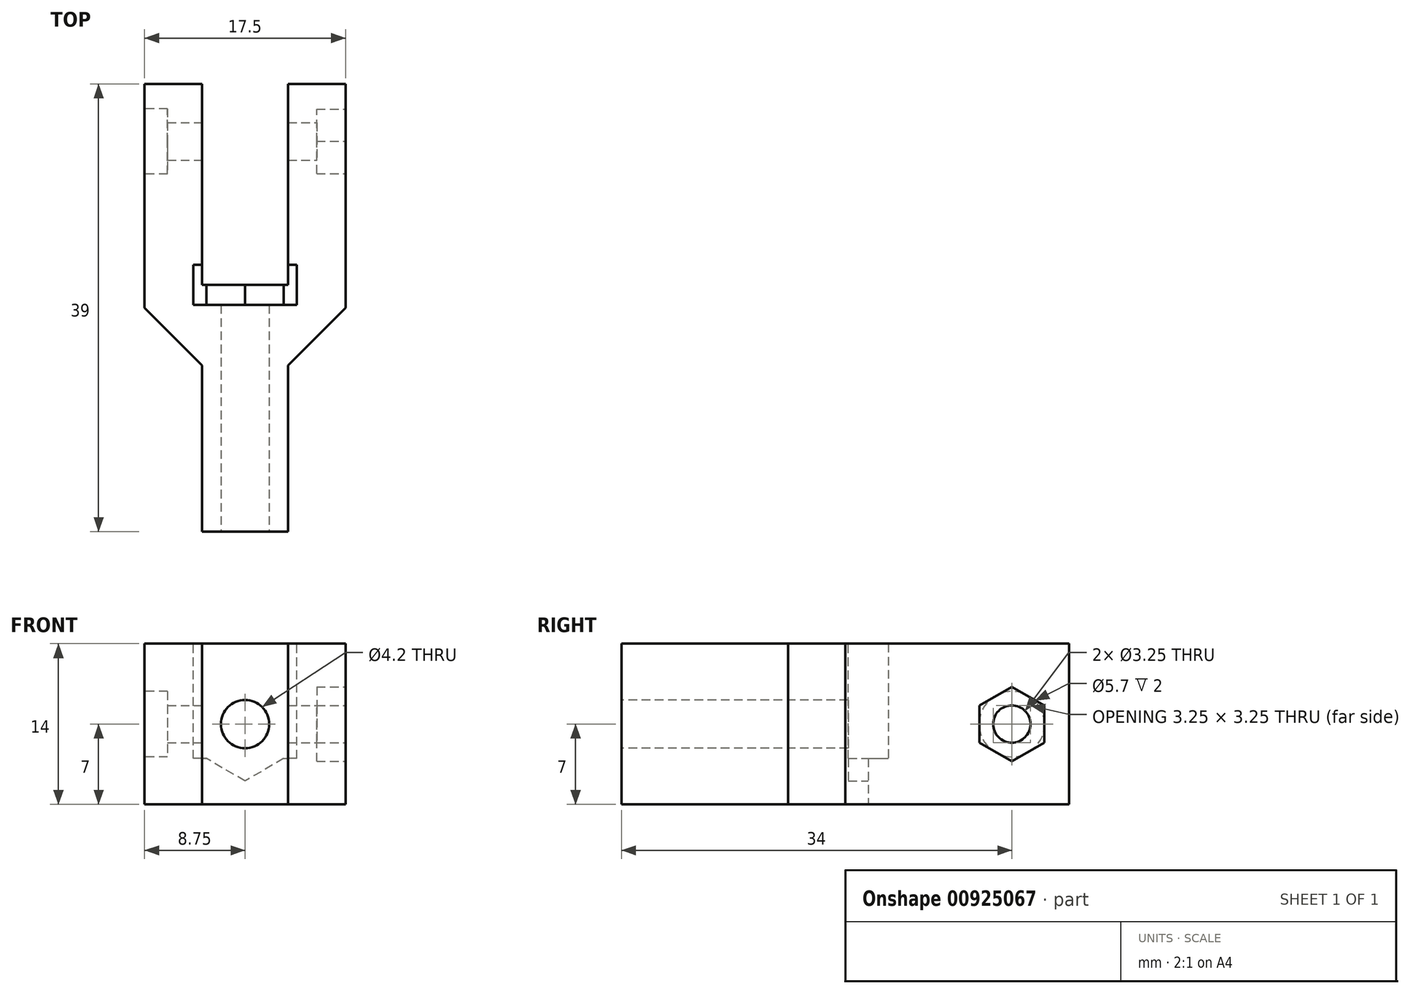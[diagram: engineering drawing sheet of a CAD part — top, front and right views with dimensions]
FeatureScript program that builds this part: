
annotation { "Feature Type Name" : "Feature", "Feature Type Description" : "" }
export const myFeature = defineFeature(function(context is Context, id is Id, definition is map)
    precondition{}
    {
        {
            var Q0;
            Q0=qCreatedBy(makeId("Top.planeOp"),FACE);
            var sketch = newSketch(context, id + "F0", { "sketchPlane" : qUnion([Q0])});
            skLineSegment(sketch, "E0.bottom", {"start": v(0, 0) * mm, "end": v(17.5, 0) * mm});
            skLineSegment(sketch, "E0.top", {"start": v(0, -39) * mm, "end": v(17.5, -39) * mm});
            skLineSegment(sketch, "E0.left", {"start": v(0, 0) * mm, "end": v(0, -39) * mm});
            skLineSegment(sketch, "E0.right", {"start": v(17.5, 0) * mm, "end": v(17.5, -39) * mm});
            skLineSegment(sketch, "E1", {"start": v(0, 0) * mm, "end": v(5, 0) * mm});
            skLineSegment(sketch, "E2", {"start": v(5, 0) * mm, "end": v(5, -17.5) * mm});
            skLineSegment(sketch, "E3", {"start": v(5, -17.5) * mm, "end": v(12.5, -17.5) * mm});
            skLineSegment(sketch, "E4", {"start": v(12.5, -17.5) * mm, "end": v(12.5, 0) * mm});
            skLineSegment(sketch, "E5", {"start": v(12.5, 0) * mm, "end": v(17.5, 0) * mm});
            skLineSegment(sketch, "E6", {"start": v(0, -19.5) * mm, "end": v(5, -24.5) * mm});
            skLineSegment(sketch, "E7", {"start": v(5, -24.5) * mm, "end": v(5, -39) * mm});
            skLineSegment(sketch, "E8", {"start": v(5, -39) * mm, "end": v(12.5, -39) * mm});
            skLineSegment(sketch, "E9", {"start": v(12.5, -39) * mm, "end": v(12.5, -24.5) * mm});
            skLineSegment(sketch, "E10", {"start": v(12.5, -24.5) * mm, "end": v(17.5, -19.5) * mm});
            skSolve(sketch);
        }
        {
            var Q0;
            {var subQ0=sQuery(id+"F0.wireOp",EDGE,"E2");Q0=makeQuery(id+"F0.imprint","IMPRINT",FACE,{"disambiguationData":[TD([[makeQuery(id+"F0.imprint","IMPRINT",EDGE,{"derivedFrom":subQ0}),-1.0]])]});}
            extrude(context, id + "F1", {"entities" : qUnion([Q0]), "depth" : 14 * mm, "offsetDistance" : 25 * mm});
        }
        {
            var Q0;
            Q0=makeQuery(id+"F1.opExtrude","SWEPT_FACE",FACE,{"disambiguationData":[OSD([sQuery(id+"F0.wireOp",EDGE,"E0.top")])]});
            var sketch = newSketch(context, id + "F2", { "sketchPlane" : qUnion([Q0])});
            skCircle(sketch, "E11", {"center": v(8.75, 7) * mm, "radius": 2.1 * mm});
            skPoint(sketch, "E11.centerSnap0", {"position": v(5, 7) * mm});
            skPoint(sketch, "E11.centerSnap1", {"position": v(8.75, 0) * mm});
            skSolve(sketch);
        }
        {
            var Q0;
            Q0 = qSketchRegion(id + "F2", true);
            extrude(context, id + "F3", {"entities" : qUnion([Q0]), "operationType" : NewBodyOperationType.REMOVE, "oppositeDirection" : true, "depth" : 25 * mm, "offsetDistance" : 25 * mm});
        }
        {
            var Q0;
            Q0=makeQuery(id+"F1.opExtrude","SWEPT_FACE",FACE,{"disambiguationData":[OSD([sQuery(id+"F0.wireOp",EDGE,"E3")])]});
            var sketch = newSketch(context, id + "F4", { "sketchPlane" : qUnion([Q0])});
            skCircle(sketch, "E12", {"center": v(-8.75, 7) * mm, "radius": 4.95 * mm});
            skLineSegment(sketch, "E13", {"start": v(-13.04, 9.48) * mm, "end": v(-13.04, 4.52) * mm});
            skLineSegment(sketch, "E14", {"start": v(-13.04, 4.52) * mm, "end": v(-8.75, 2.05) * mm});
            skLineSegment(sketch, "E15", {"start": v(-8.75, 2.05) * mm, "end": v(-4.46, 4.52) * mm});
            skLineSegment(sketch, "E16", {"start": v(-4.46, 4.52) * mm, "end": v(-4.46, 9.48) * mm});
            skLineSegment(sketch, "E17", {"start": v(-4.46, 9.48) * mm, "end": v(-8.75, 11.95) * mm});
            skLineSegment(sketch, "E18", {"start": v(-8.75, 11.95) * mm, "end": v(-13.04, 9.48) * mm});
            skSolve(sketch);
        }
        {
            var Q0;
            Q0=makeQuery(id+"F1.opExtrude","CAP_FACE",FACE,{"disambiguationData":[OSD([sQuery(id+"F0.wireOp",EDGE,"E0.bottom"),sQuery(id+"F0.wireOp",EDGE,"E0.top"),sQuery(id+"F0.wireOp",EDGE,"E0.left"),sQuery(id+"F0.wireOp",EDGE,"E0.right"),sQuery(id+"F0.wireOp",EDGE,"E2"),sQuery(id+"F0.wireOp",EDGE,"E3"),sQuery(id+"F0.wireOp",EDGE,"E4"),sQuery(id+"F0.wireOp",EDGE,"E6"),sQuery(id+"F0.wireOp",EDGE,"E7"),sQuery(id+"F0.wireOp",EDGE,"E9"),sQuery(id+"F0.wireOp",EDGE,"E10")])],"isStart":false});
            var sketch = newSketch(context, id + "F5", { "sketchPlane" : qUnion([Q0])});
            skLineSegment(sketch, "E19.bottom", {"start": v(13.25, -19.25) * mm, "end": v(4.25, -19.25) * mm});
            skLineSegment(sketch, "E19.top", {"start": v(13.25, -15.75) * mm, "end": v(4.25, -15.75) * mm});
            skLineSegment(sketch, "E19.left", {"start": v(13.25, -19.25) * mm, "end": v(13.25, -15.75) * mm});
            skLineSegment(sketch, "E19.right", {"start": v(4.25, -19.25) * mm, "end": v(4.25, -15.75) * mm});
            skSolve(sketch);
        }
        {
            var Q0;
            Q0 = qSketchRegion(id + "F5", true);
            extrude(context, id + "F6", {"entities" : qUnion([Q0]), "operationType" : NewBodyOperationType.REMOVE, "oppositeDirection" : true, "depth" : 10 * mm, "offsetDistance" : 25 * mm});
        }
        {
            var Q0;
            {var subQ4=sQuery(id+"F0.wireOp",EDGE,"E3");Q0=makeQuery(id+"F4.imprint","IMPRINT",FACE,{"disambiguationData":[TD([[makeQuery(id+"F4.imprint","IMPRINT",EDGE,{"derivedFrom":makeQuery(id+"F3.boolean.opBoolean","INTERSECT",EDGE,{"derivedFrom":[makeQuery(id+"F1.opExtrude","SWEPT_FACE",FACE,{"disambiguationData":[OSD([subQ4])]}),makeQuery(id+"F3.opExtrude","SWEPT_FACE",FACE,{"disambiguationData":[OSD([sQuery(id+"F2.wireOp",EDGE,"E11")])]})]})}),-1.0]])]});}
            extrude(context, id + "F7", {"entities" : qUnion([Q0]), "operationType" : NewBodyOperationType.REMOVE, "oppositeDirection" : true, "depth" : 1.75 * mm, "offsetDistance" : 25 * mm});
        }
        {
            var Q0;
            Q0=makeQuery(id+"F1.opExtrude","SWEPT_FACE",FACE,{"disambiguationData":[OSD([sQuery(id+"F0.wireOp",EDGE,"E0.right")])]});
            var sketch = newSketch(context, id + "F8", { "sketchPlane" : qUnion([Q0])});
            skCircle(sketch, "E20", {"center": v(-5, 7) * mm, "radius": 1.63 * mm});
            skPoint(sketch, "E20.centerSnap0", {"position": v(0, 7) * mm});
            skCircle(sketch, "E21", {"center": v(-5, 7) * mm, "radius": 3.25 * mm});
            skLineSegment(sketch, "E22", {"start": v(-5, 10.25) * mm, "end": v(-2.19, 8.62) * mm});
            skLineSegment(sketch, "E23", {"start": v(-2.19, 8.62) * mm, "end": v(-2.19, 5.38) * mm});
            skLineSegment(sketch, "E24", {"start": v(-2.19, 5.38) * mm, "end": v(-5, 3.75) * mm});
            skLineSegment(sketch, "E25", {"start": v(-5, 3.75) * mm, "end": v(-7.81, 5.38) * mm});
            skLineSegment(sketch, "E26", {"start": v(-7.81, 5.38) * mm, "end": v(-7.81, 8.62) * mm});
            skLineSegment(sketch, "E27", {"start": v(-7.81, 8.62) * mm, "end": v(-5, 10.25) * mm});
            skSolve(sketch);
        }
        {
            var Q0;
            Q0=makeQuery(id+"F8.imprint","IMPRINT",FACE,{"disambiguationData":[TD([[makeQuery(id+"F8.imprint","IMPRINT",EDGE,{"derivedFrom":sQuery(id+"F8.wireOp",EDGE,"E20")}),-1.0]])]});
            extrude(context, id + "F9", {"entities" : qUnion([Q0]), "operationType" : NewBodyOperationType.REMOVE, "oppositeDirection" : true, "depth" : 2.5 * mm, "offsetDistance" : 25 * mm});
        }
        {
            var Q0;
            Q0=makeQuery(id+"F9.boolean.opBoolean","SPLIT",FACE,{"disambiguationData":[TD([makeQuery(id+"F9.opExtrude","SWEPT_FACE",FACE,{"disambiguationData":[OSD([sQuery(id+"F8.wireOp",EDGE,"E20")])]})])],"derivedFrom":makeQuery(id+"F1.opExtrude","SWEPT_FACE",FACE,{"disambiguationData":[OSD([sQuery(id+"F0.wireOp",EDGE,"E0.right")])]})});
            extrude(context, id + "F10", {"entities" : qUnion([Q0]), "operationType" : NewBodyOperationType.REMOVE, "oppositeDirection" : true, "depth" : 25 * mm, "offsetDistance" : 25 * mm});
        }
        {
            var Q0;
            Q0=makeQuery(id+"F1.opExtrude","SWEPT_FACE",FACE,{"disambiguationData":[OSD([sQuery(id+"F0.wireOp",EDGE,"E0.left")])]});
            var sketch = newSketch(context, id + "F11", { "sketchPlane" : qUnion([Q0])});
            skCircle(sketch, "E28", {"center": v(5, 7) * mm, "radius": 2.85 * mm});
            skSolve(sketch);
        }
        {
            var Q0;
            Q0=makeQuery(id+"F11.imprint","IMPRINT",FACE,{"disambiguationData":[TD([[makeQuery(id+"F11.imprint","IMPRINT",EDGE,{"derivedFrom":sQuery(id+"F11.wireOp",EDGE,"E28")}),1.0]])]});
            var Q1;
            Q1=makeQuery(id+"F11.imprint","IMPRINT",FACE,{"disambiguationData":[TD([[makeQuery(id+"F11.imprint","IMPRINT",EDGE,{"derivedFrom":makeQuery(id+"F10.boolean.opBoolean","INTERSECT",EDGE,{"derivedFrom":[makeQuery(id+"F1.opExtrude","SWEPT_FACE",FACE,{"disambiguationData":[OSD([sQuery(id+"F0.wireOp",EDGE,"E0.left")])]}),makeQuery(id+"F10.opExtrude","SWEPT_FACE",FACE,{"disambiguationData":[OSD([sQuery(id+"F8.wireOp",EDGE,"E20")])]})]})}),-1.0]])]});
            extrude(context, id + "F12", {"entities" : qUnion([Q0, Q1]), "operationType" : NewBodyOperationType.REMOVE, "oppositeDirection" : true, "depth" : 2 * mm, "offsetDistance" : 25 * mm});
        }
    });
